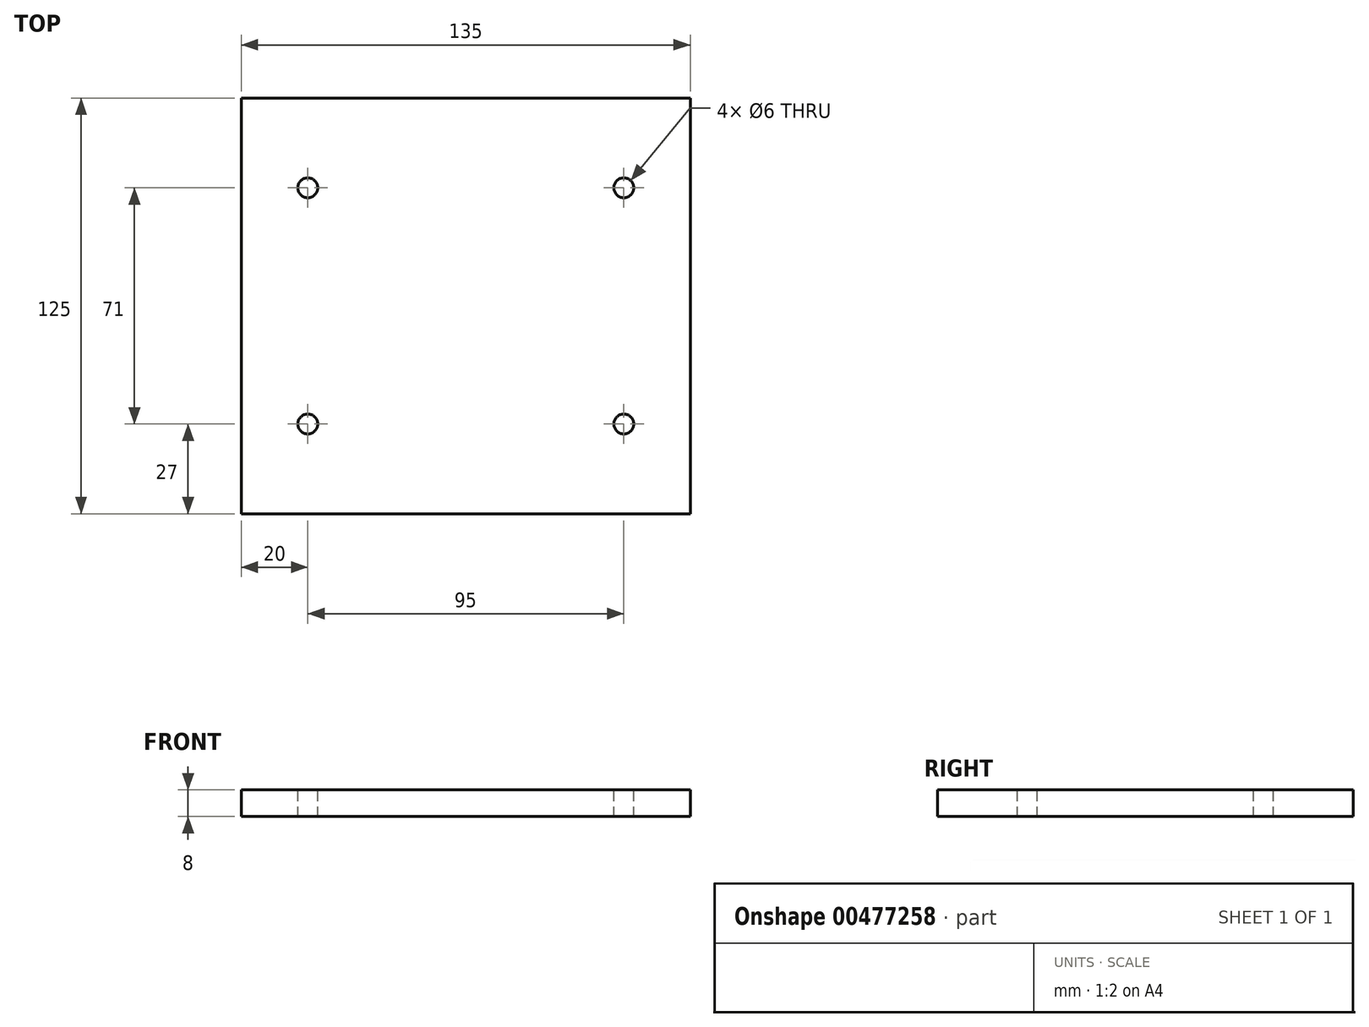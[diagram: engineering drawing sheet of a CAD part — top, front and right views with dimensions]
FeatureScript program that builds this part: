
annotation { "Feature Type Name" : "Feature", "Feature Type Description" : "" }
export const myFeature = defineFeature(function(context is Context, id is Id, definition is map)
    precondition{}
    {
        {
            var Q0;
            Q0=qCreatedBy(makeId("Top.planeOp"),FACE);
            var sketch = newSketch(context, id + "F0", { "sketchPlane" : qUnion([Q0])});
            skLineSegment(sketch, "E0.bottom", {"start": v(67.5, 62.5) * mm, "end": v(-67.5, 62.5) * mm});
            skLineSegment(sketch, "E0.top", {"start": v(67.5, -62.5) * mm, "end": v(-67.5, -62.5) * mm});
            skLineSegment(sketch, "E0.left", {"start": v(67.5, 62.5) * mm, "end": v(67.5, -62.5) * mm});
            skLineSegment(sketch, "E0.right", {"start": v(-67.5, 62.5) * mm, "end": v(-67.5, -62.5) * mm});
            skPoint(sketch, "E0.middle", {"position": v(0, 0) * mm});
            skLineSegment(sketch, "E1.bottom", {"start": v(47.5, 32.5) * mm, "end": v(-47.5, 32.5) * mm});
            skLineSegment(sketch, "E1.top", {"start": v(47.5, -32.5) * mm, "end": v(-47.5, -32.5) * mm});
            skLineSegment(sketch, "E1.left", {"start": v(47.5, 32.5) * mm, "end": v(47.5, -32.5) * mm});
            skLineSegment(sketch, "E1.right", {"start": v(-47.5, 32.5) * mm, "end": v(-47.5, -32.5) * mm});
            skPoint(sketch, "E2", {"position": v(47.5, 35.5) * mm});
            skPoint(sketch, "E3", {"position": v(-47.5, 35.5) * mm});
            skPoint(sketch, "E4", {"position": v(-47.5, -35.5) * mm});
            skPoint(sketch, "E5", {"position": v(47.5, -35.5) * mm});
            skSolve(sketch);
        }
        {
            var Q0;
            Q0=makeQuery(id+"F0.imprint","IMPRINT",FACE,{"disambiguationData":[TD([[makeQuery(id+"F0.imprint","IMPRINT",EDGE,{"derivedFrom":sQuery(id+"F0.wireOp",EDGE,"E0.bottom")}),1.0]])]});
            var Q1;
            Q1=makeQuery(id+"F0.imprint","IMPRINT",FACE,{"disambiguationData":[TD([[makeQuery(id+"F0.imprint","IMPRINT",EDGE,{"derivedFrom":sQuery(id+"F0.wireOp",EDGE,"E1.bottom")}),1.0]])]});
            extrude(context, id + "F1", {"entities" : qUnion([Q0, Q1]), "depth" : 8 * mm});
        }
        {
            var Q0;
            Q0=makeQuery(id+"F1.opExtrude","CAP_FACE",FACE,{"disambiguationData":[OSD([sQuery(id+"F0.wireOp",EDGE,"E0.bottom"),sQuery(id+"F0.wireOp",EDGE,"E0.top"),sQuery(id+"F0.wireOp",EDGE,"E0.left"),sQuery(id+"F0.wireOp",EDGE,"E0.right")])],"isStart":false});
            var sketch = newSketch(context, id + "F2", { "sketchPlane" : qUnion([Q0])});
            skLineSegment(sketch, "E6.bottom", {"start": v(47.5, 32.5) * mm, "end": v(-47.5, 32.5) * mm});
            skLineSegment(sketch, "E6.top", {"start": v(47.5, -32.5) * mm, "end": v(-47.5, -32.5) * mm});
            skLineSegment(sketch, "E6.left", {"start": v(47.5, 32.5) * mm, "end": v(47.5, -32.5) * mm});
            skLineSegment(sketch, "E6.right", {"start": v(-47.5, 32.5) * mm, "end": v(-47.5, -32.5) * mm});
            skPoint(sketch, "E6.middle", {"position": v(0, 0) * mm});
            skPoint(sketch, "E7", {"position": v(47.5, 35.5) * mm});
            skPoint(sketch, "E8", {"position": v(-47.5, 35.5) * mm});
            skPoint(sketch, "E9", {"position": v(-47.5, -35.5) * mm});
            skPoint(sketch, "E10", {"position": v(47.5, -35.5) * mm});
            skSolve(sketch);
        }
        {
            var Q0;
            Q0=sQuery(id+"F2.wireOp",VERTEX,"E10");
            var Q1;
            Q1=sQuery(id+"F2.wireOp",VERTEX,"E9");
            var Q2;
            Q2=sQuery(id+"F2.wireOp",VERTEX,"E8");
            var Q3;
            Q3=sQuery(id+"F2.wireOp",VERTEX,"E7");
            var Q4;
            Q4=makeQuery(id+"F1.opExtrude","SWEPT_BODY",BODY,{"disambiguationData":[OSD([sQuery(id+"F0.wireOp",EDGE,"E0.bottom"),sQuery(id+"F0.wireOp",EDGE,"E0.top"),sQuery(id+"F0.wireOp",EDGE,"E0.left"),sQuery(id+"F0.wireOp",EDGE,"E0.right")])]});
            hole(context, id + "F3", {"style" : HoleStyle.SIMPLE, "endStyle" : HoleEndStyle.THROUGH, "holeDiameter" : 6 * mm, "isTappedThrough" : true, "tappedDepth" : 12 * mm, "tapClearance" : 3, "locations" : qUnion([Q0, Q1, Q2, Q3]), "scope" : qUnion([Q4])});
        }
    });
